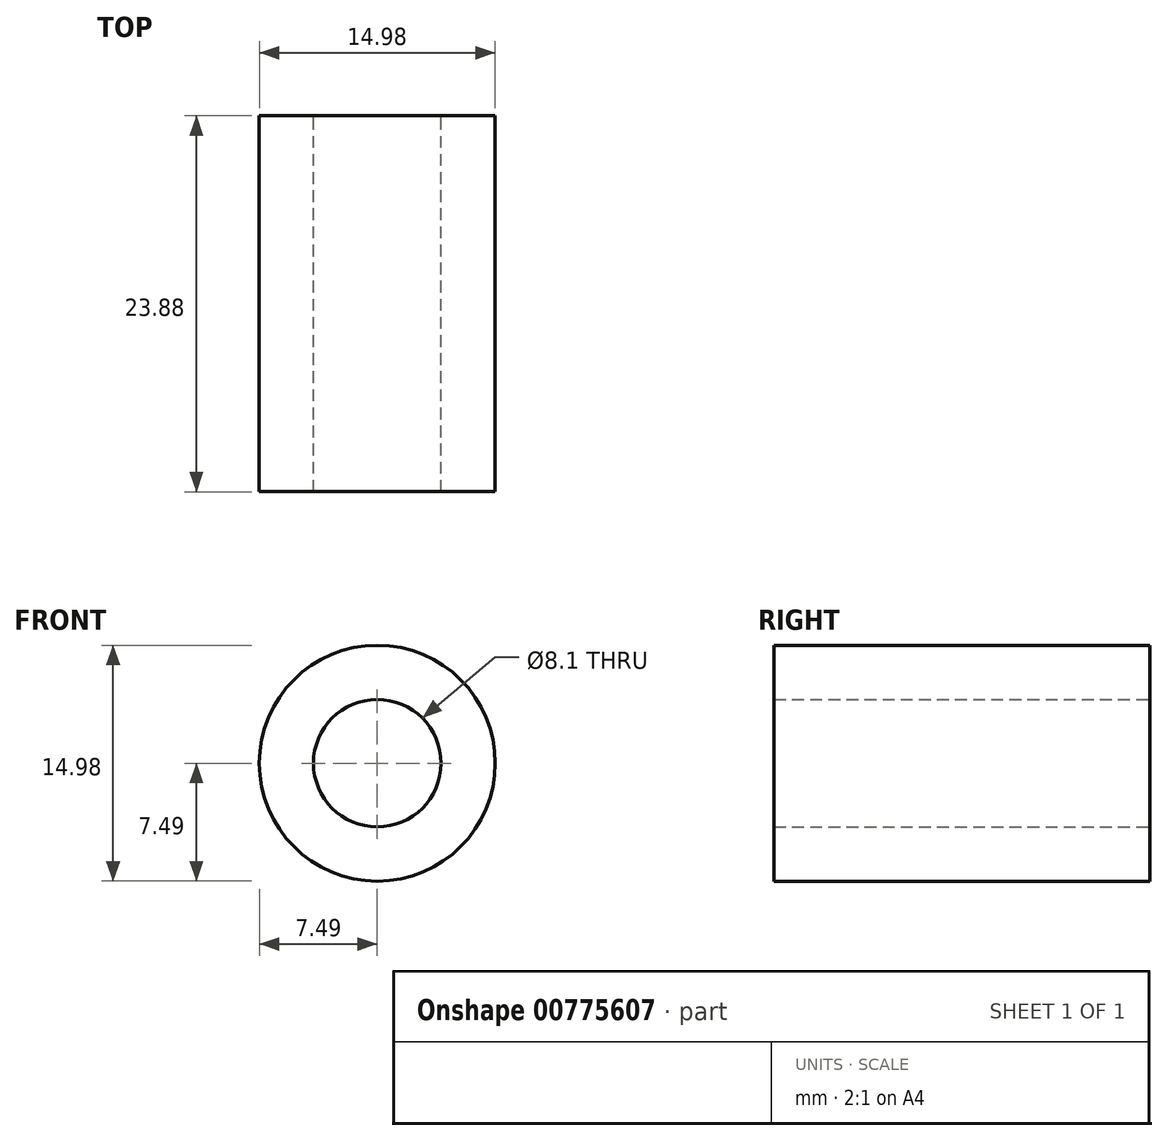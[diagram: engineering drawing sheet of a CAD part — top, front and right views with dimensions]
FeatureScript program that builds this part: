
annotation { "Feature Type Name" : "Feature", "Feature Type Description" : "" }
export const myFeature = defineFeature(function(context is Context, id is Id, definition is map)
    precondition{}
    {
        {
            var Q0;
            Q0=qCreatedBy(makeId("Front.planeOp"),FACE);
            var sketch = newSketch(context, id + "F0", { "sketchPlane" : qUnion([Q0])});
            skCircle(sketch, "E0", {"center": v(0, 0) * mm, "radius": 7.5 * mm});
            skCircle(sketch, "E1", {"center": v(0, 0) * mm, "radius": 4.05 * mm});
            skSolve(sketch);
        }
        {
            var Q0;
            Q0 = qSketchRegion(id + "F0", true);
            extrude(context, id + "F1", {"entities" : qUnion([Q0]), "depth" : 23.88 * mm, "offsetDistance" : 25.4 * mm});
        }
    });
